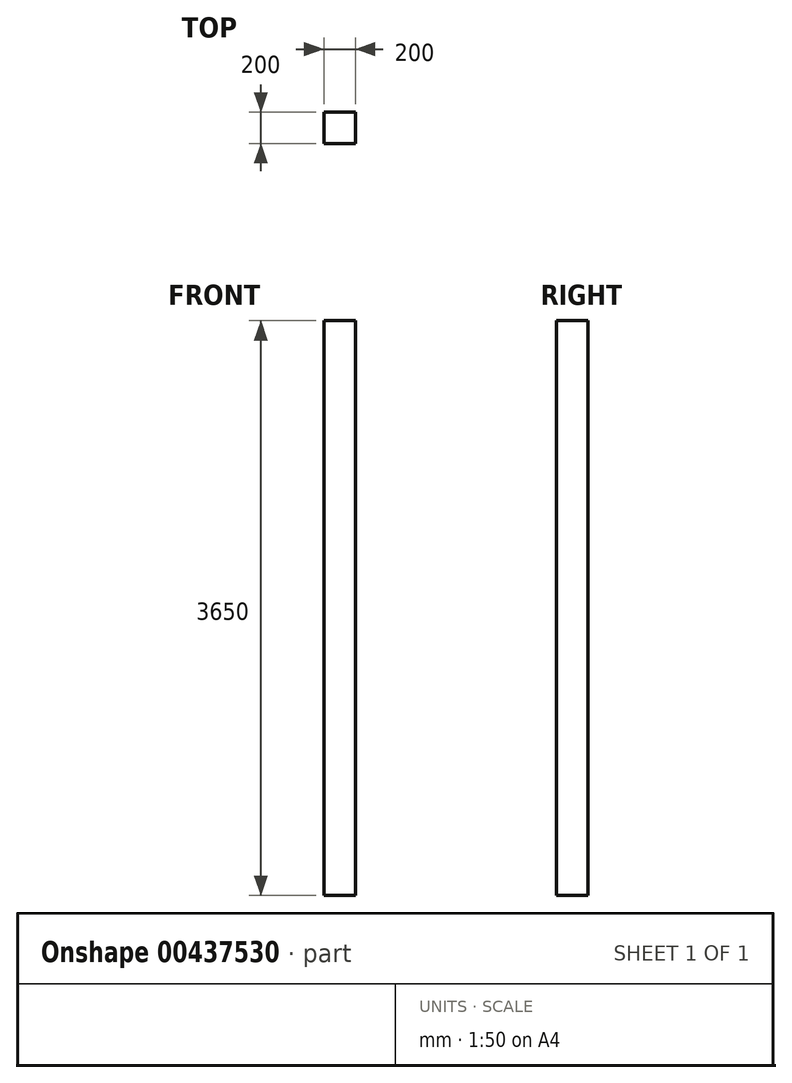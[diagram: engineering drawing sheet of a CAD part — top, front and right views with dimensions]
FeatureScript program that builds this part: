
annotation { "Feature Type Name" : "Feature", "Feature Type Description" : "" }
export const myFeature = defineFeature(function(context is Context, id is Id, definition is map)
    precondition{}
    {
        {
            var Q0;
            Q0=qCreatedBy(makeId("Top.planeOp"),FACE);
            var sketch = newSketch(context, id + "F0", { "sketchPlane" : qUnion([Q0])});
            skLineSegment(sketch, "E0.bottom", {"start": v(-100, 100) * mm, "end": v(100, 100) * mm});
            skLineSegment(sketch, "E0.top", {"start": v(-100, -100) * mm, "end": v(100, -100) * mm});
            skLineSegment(sketch, "E0.left", {"start": v(-100, 100) * mm, "end": v(-100, -100) * mm});
            skLineSegment(sketch, "E0.right", {"start": v(100, 100) * mm, "end": v(100, -100) * mm});
            skPoint(sketch, "E0.middle", {"position": v(0, 0) * mm});
            skSolve(sketch);
        }
        {
            var Q0;
            Q0 = qSketchRegion(id + "F0", true);
            extrude(context, id + "F1", {"entities" : qUnion([Q0]), "depth" : 3650 * mm});
        }
    });
